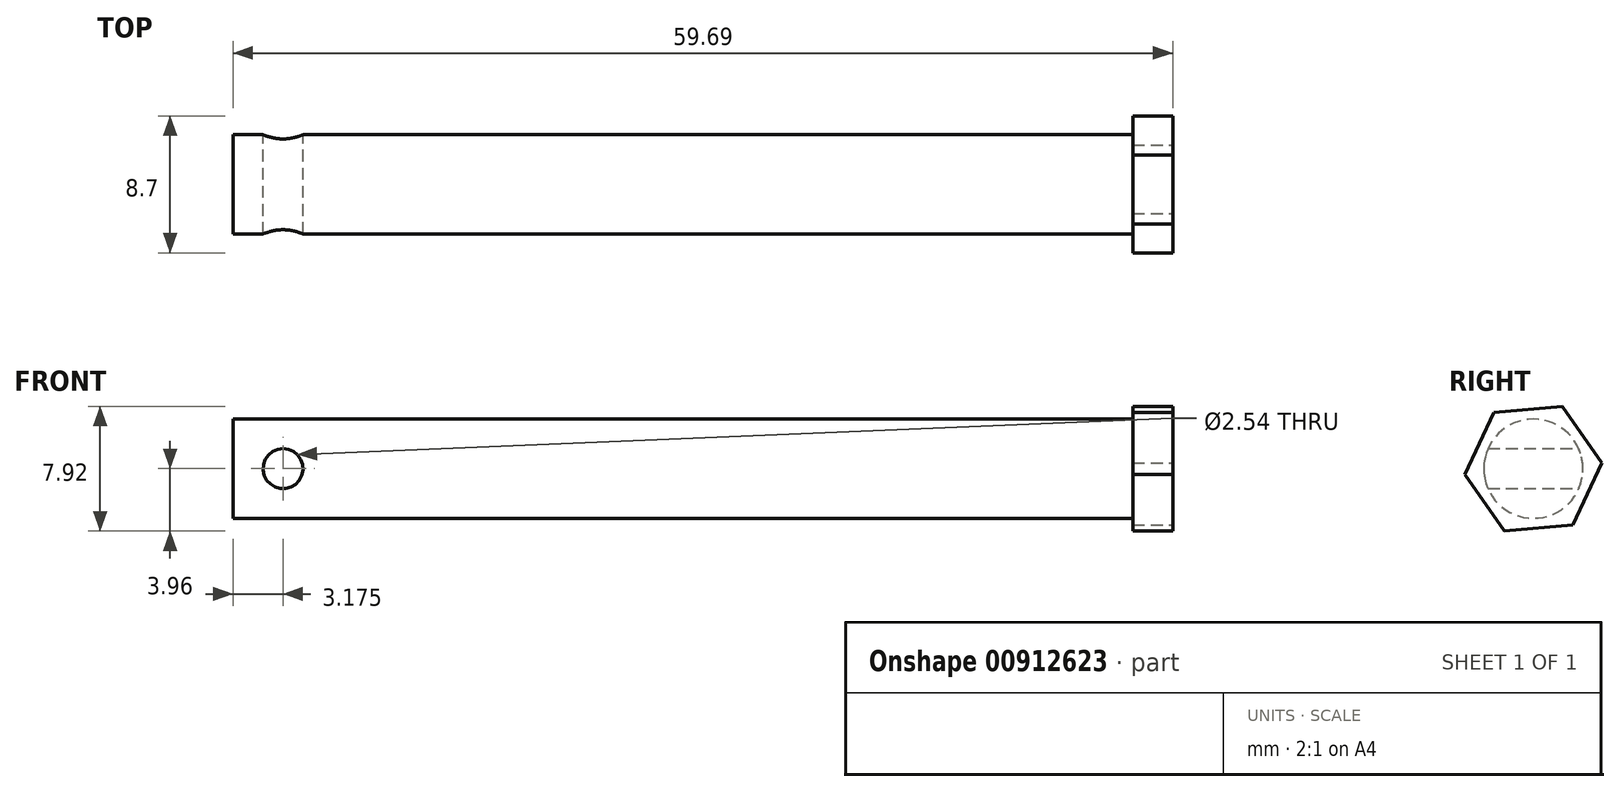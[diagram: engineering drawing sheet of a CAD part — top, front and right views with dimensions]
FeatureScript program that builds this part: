
annotation { "Feature Type Name" : "Feature", "Feature Type Description" : "" }
export const myFeature = defineFeature(function(context is Context, id is Id, definition is map)
    precondition{}
    {
        {
            var Q0;
            Q0=qCreatedBy(makeId("Right.planeOp"),FACE);
            var sketch = newSketch(context, id + "F0", { "sketchPlane" : qUnion([Q0])});
            skCircle(sketch, "E0", {"center": v(0, 0) * mm, "radius": 3.15 * mm});
            skSolve(sketch);
        }
        {
            var Q0;
            Q0 = qSketchRegion(id + "F0", true);
            extrude(context, id + "F1", {"entities" : qUnion([Q0]), "depth" : 59.69 * mm, "offsetDistance" : 25.4 * mm});
        }
        {
            var Q0;
            Q0=qCreatedBy(makeId("Front.planeOp"),FACE);
            var sketch = newSketch(context, id + "F2", { "sketchPlane" : qUnion([Q0])});
            skCircle(sketch, "E1", {"center": v(3.18, 0) * mm, "radius": 1.27 * mm});
            skSolve(sketch);
        }
        {
            var Q0;
            Q0 = qSketchRegion(id + "F2", true);
            extrude(context, id + "F3", {"entities" : qUnion([Q0]), "operationType" : NewBodyOperationType.REMOVE, "depth" : 17.27 * mm, "offsetDistance" : 25.4 * mm});
        }
        {
            var Q0;
            Q0=makeQuery(id+"F1.opExtrude","CAP_FACE",FACE,{"disambiguationData":[OSD([sQuery(id+"F0.wireOp",EDGE,"E0")])],"isStart":false});
            var sketch = newSketch(context, id + "F4", { "sketchPlane" : qUnion([Q0])});
            skCircle(sketch, "E2.cCircle", {"center": v(0, 0) * mm, "radius": 3.78 * mm, "construction": true});
            skLineSegment(sketch, "E2.0", {"start": v(4.35, 0.38) * mm, "end": v(2.5, -3.58) * mm});
            skLineSegment(sketch, "E2.1", {"start": v(2.5, -3.58) * mm, "end": v(-1.85, -3.96) * mm});
            skLineSegment(sketch, "E2.2", {"start": v(-1.85, -3.96) * mm, "end": v(-4.35, -0.38) * mm});
            skLineSegment(sketch, "E2.3", {"start": v(-4.35, -0.38) * mm, "end": v(-2.5, 3.58) * mm});
            skLineSegment(sketch, "E2.4", {"start": v(-2.5, 3.58) * mm, "end": v(1.85, 3.96) * mm});
            skLineSegment(sketch, "E2.5", {"start": v(1.85, 3.96) * mm, "end": v(4.35, 0.38) * mm});
            skPoint(sketch, "E2.0.midPoint", {"position": v(3.43, -1.6) * mm});
            skSolve(sketch);
        }
        {
            var Q0;
            Q0=makeQuery(id+"F4.imprint","IMPRINT",FACE,{"disambiguationData":[TD([[makeQuery(id+"F4.imprint","IMPRINT",EDGE,{"derivedFrom":sQuery(id+"F4.wireOp",EDGE,"E2.0")}),-1.0]])]});
            extrude(context, id + "F5", {"entities" : qUnion([Q0]), "operationType" : NewBodyOperationType.ADD, "oppositeDirection" : true, "depth" : 2.54 * mm, "offsetDistance" : 25.4 * mm});
        }
        {
            var Q0;
            Q0 = qSketchRegion(id + "F2", true);
            extrude(context, id + "F6", {"entities" : qUnion([Q0]), "operationType" : NewBodyOperationType.REMOVE, "oppositeDirection" : true, "depth" : 14.25 * mm, "offsetDistance" : 25.4 * mm});
        }
    });
